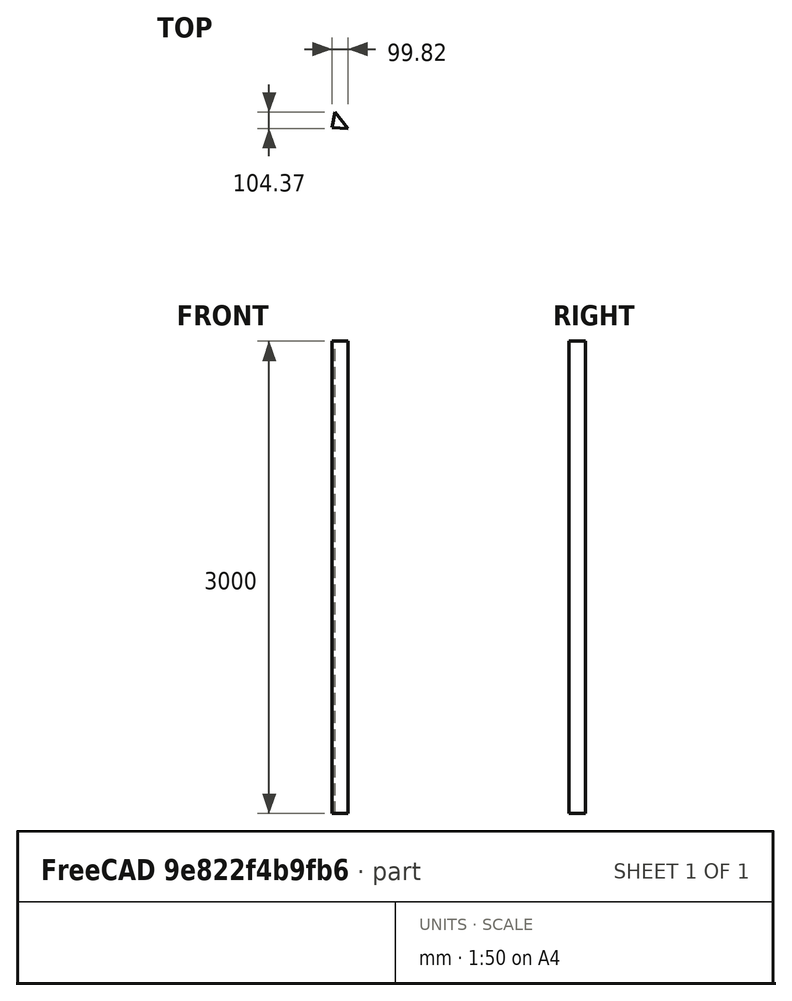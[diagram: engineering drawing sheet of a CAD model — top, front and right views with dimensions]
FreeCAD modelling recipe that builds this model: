
FCSTD DOCUMENT  (FreeCAD 0.20R29603 (Git))
Label: 20220524-freecad-arch-learning
License: All rights reserved
LicenseURL: http://en.wikipedia.org/wiki/All_rights_reserved
objects: Part::Part2DObjectPython×1, Part::FeaturePython×1
note: 2 computed .brp shape members not serialized (recipe doc carries the construction recipe); baked Part::Feature solids carry a one-line shape summary decoded from their .brp

FEATURE [Part::Part2DObjectPython] Rectangle  # Draft 2D object (typed FeaturePython)
  Area = 0
  ChamferSize = 0
  Columns = 1
  FilletRadius = 0
  Height = 3000
  Length = 4000
  MakeFace = false
  Placement = pos=(-1483.41,-1715.49,1245.25) rot=(-0.79919,0.556625,-0.226856;0.516311rad)
  Rows = 1
FEATURE [Part::FeaturePython] Wall  # Arch/BIM 166 (typed FeaturePython)
  Align = 2
  Area = 42000000
  Base = -> Rectangle
  BlockHeight = 0
  BlockLength = 0
  CountBroken = 0
  CountEntire = 0
  Face = 0
  Height = 3000
  HorizontalArea = 4965.67
  IfcData = attributes={"GlobalId": {"name": "GlobalId", "type": "IfcGloballyUniqueId", "is_enum": false, "enum_values": []}, "Description": {"... (+533 chars omitted),+1 more (map truncated)
  IfcType = 166
  Joint = 0
  Length = 14000
  MakeBlocks = false
  MoveBase = false
  MoveWithHost = false
  Normal = (0,0,0)
  OffsetFirst = 0
  OffsetSecond = 0
  PerimeterLength = 332.892
  PredefinedType = 0
  VerticalArea = 998677
  Width = 200
